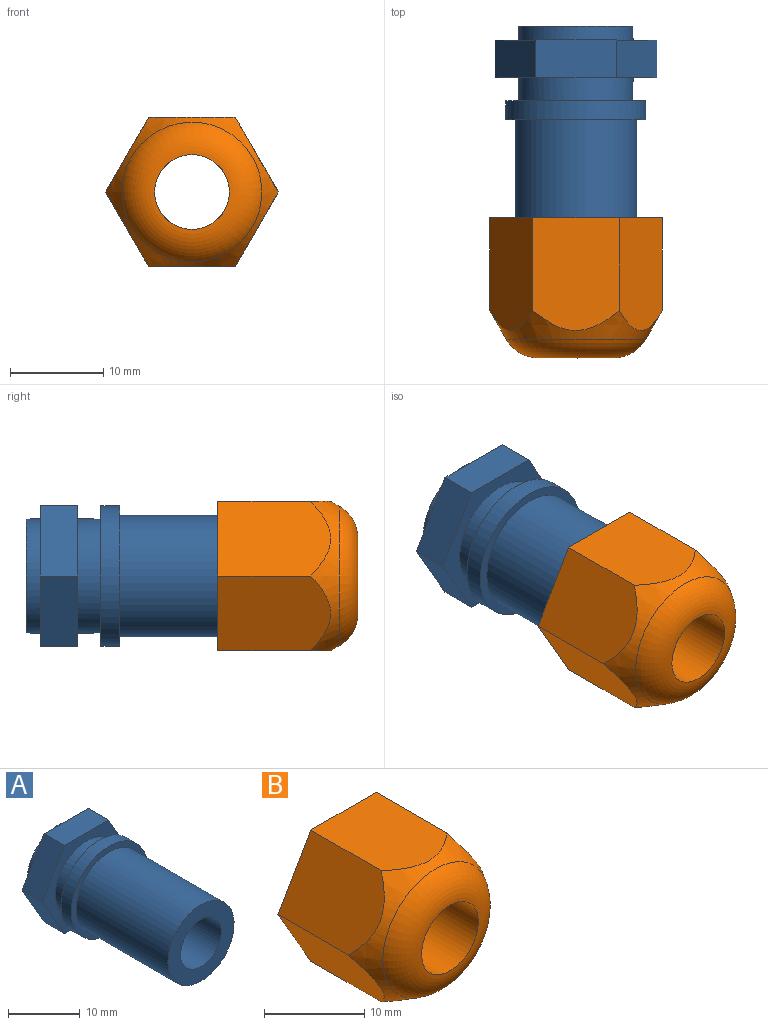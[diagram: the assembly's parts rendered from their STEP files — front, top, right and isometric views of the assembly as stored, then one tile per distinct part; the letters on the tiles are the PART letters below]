
ASSEMBLY  parts=2 mates=1
PART A: 17 faces, bbox 17.3x28x15 mm
  f0: cylinder r=6.1mm len=12.2mm, axis (0,1,0), area 57.5mm2, adj f7,f15
  f1: plane 13x13mm, normal (0,-1,0), area 82.5mm2, adj f2,f8
  f2: cylinder r=6.5mm len=18mm, axis (0,1,0), area 735.1mm2, adj f1,f3
  f3: plane 15x15mm, normal (0,-1,0), area 44mm2, adj f2,f4
  f4: cylinder r=7.5mm len=15mm, axis (0,1,0), area 94.2mm2, adj f3,f5
  f5: plane 15x15mm, normal (0,1,0), area 59.8mm2, adj f4,f6
  f6: cylinder r=6.1mm len=12.2mm, axis (0,1,0), area 95.8mm2, adj f5,f16
  f7: plane 12.2x12.2mm, normal (0,1,0), area 66.6mm2, adj f0,f8
  f8: cylinder r=4mm len=28mm, axis (0,1,0), area 703.7mm2, adj f1,f7
  f9: plane 7.5x4.33mm, normal (0.87,0,-0.5), area 34.6mm2, adj f10,f14,f15,f16
  f10: plane 8.66x4mm, normal (0,0,-1), area 34.6mm2, adj f9,f11,f15,f16
  f11: plane 7.5x4.33mm, normal (-0.87,0,-0.5), area 34.6mm2, adj f10,f12,f15,f16
  f12: plane 7.5x4.33mm, normal (-0.87,0,0.5), area 34.6mm2, adj f11,f13,f15,f16
  f13: plane 8.66x4mm, normal (0,0,1), area 34.6mm2, adj f12,f14,f15,f16
  f14: plane 7.5x4.33mm, normal (0.87,0,0.5), area 34.6mm2, adj f9,f13,f15,f16
  f15: plane 17.32x15mm, normal (0,1,0), area 78mm2, adj f0,f9,f10,f11,f12,f13,f14
  f16: plane 17.32x15mm, normal (0,-1,0), area 78mm2, adj f6,f9,f10,f11,f12,f13,f14
PART B: 10 faces, bbox 18.5x15x18.5 mm
  f0: plane 18.48x16mm, normal (0,1,0), area 171.4mm2, adj f1,f2,f3,f4,f5,f6,f7
  f1: plane 12.08x8mm, normal (0.87,0,0.5), area 104.7mm2, adj f0,f2,f6,f8
  f2: plane 12.07x9.24mm, normal (0,0,1), area 104.7mm2, adj f0,f1,f3,f8
  f3: plane 12.08x8mm, normal (-0.87,0,0.5), area 104.7mm2, adj f0,f2,f4,f8
  f4: plane 12.08x8mm, normal (-0.87,0,-0.5), area 104.7mm2, adj f0,f3,f5,f8
  f5: plane 12.07x9.24mm, normal (0,0,-1), area 104.7mm2, adj f0,f4,f6,f8
  f6: plane 12.08x8mm, normal (0.87,0,-0.5), area 104.7mm2, adj f0,f1,f5,f8
  f7: cylinder r=4mm len=15mm, axis (0,1,0), area 377mm2, adj f0,f9
  f8: cone r=7.46mm half-angle=30deg, axis (0,1,0), area 93.3mm2, adj f1,f2,f3,f4,f5,f6,f9
  f9: torus R=4mm, axis (0,1,0), area 155.5mm2, adj f7,f8
PLACE A at identity fixed
PLACE B t=(0,-5.5,0)mm
MATE cylindrical A.f0 <-> B.f7  axis (0,-1,0) through (0,-28,0)mm
